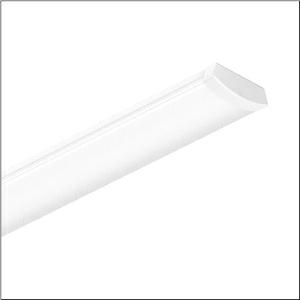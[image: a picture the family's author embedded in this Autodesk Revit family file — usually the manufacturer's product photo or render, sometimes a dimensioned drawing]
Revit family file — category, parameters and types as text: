
# Revit family: siluette_21_51ln12mdm20a
name_source: partatom
category: Lighting Fixtures
units: mm (PartAtom-declared; Revit-internal decimal feet)

## family parameters
Cut with Voids When Loaded = No
Host = Face
Light Source = No
Part Type = Normal
Room Calculation Point = No
Round Connector Dimension = Use Diameter
Shared = No

## types (1)
- --- (1 x LED, 1510 lm, 12.2 W, 5000K)
    Apparent Load = 12 VA
    CIE Flux Codes = 43 73 92 94 100
    Color Rendering = 80
    Color Temperature = 5000K
    Default Elevation = 1800 mm
    Description = Siluette 21, office luminaire, primary optical cover: enclosure, of PC, frosted, light emission: direct distribution, primary light characteristic: symmetric, installation type: suspended mounting, surface-mounted, LED, rated luminous flux: 2.630lm, luminous efficacy: 135lm/W, light colour: 830/840/850, colour temperature: 3000/4000/5000K, control gear: ON/OFF Multilumen, with terminal, 3-pole, mains connection: 220..240V, AC, 50/60Hz, rated input power: 20W, housing, of sheet steel, white, length: 600mm, width: 152mm, height: 53mm, end cap, of PMMA, white, protection rating (complete): IP44, insulation class (complete): insulation class I (protective earthing), certification: CE, UKCA, protection symbol: D, impact resistance: IK04, permissible operating ambient temperature: -20..+40°C, contact your sales advisor before using the luminaires in applications with unclear chemical exposure, large temperature fluctuations or condensation-forming humidity, corresponds to IFS (International Featured Standards) requirements for safety and quality in the food industry, packaging unit: 1 piece
    Height = 52 mm  [stored 0.170604 ft]
    Lamp = 1 x LED
    Lamp Light Flux = 1510 lm
    Lamp Power = 12.2 W
    Lamp count = 1
    Length = 645 mm
    Luminous efficacy = 124 lm/W
    Manufacturer = Siteco
    ModVariant = No
    Model = 51LN12MDM20A
    Mounting Place = Ceiling
    Mounting Type = Pendant
    Number of Poles = 1
    OnlyDefault = Yes
    Power Factor = 1
    Product Name = Siluette 21
    Product group = office luminaire | ceiling pendant
    ProductGroupID = 903
    Protection Class = Protection class I
    Protection Degree = IP 44
    RLX_Detail_Level = 1
    RLX_Emergency_Light_Flux = 0 lm
    RLX_Emergency_Type = 0
    RLX_Emergency_Type_DB = No
    RlxData = <blob elided: 19165 chars, md5=18696f39>
    Socket = socket
    Standby Power = 0 W
    System Light Flux = 1510 lm
    System Power = 12 W
    Type Comments = individual setting: colour temperature 5000K, luminous flux: 58 % | (OFF | OFF | ON) | 200 mA
    Type Image = l_1296910.jpg
    URL = http://relux.com
    VarID = @adj_067433
    Voltage = 0 V
    Weight = 0.00 kg
    Width = 152 mm

note: [stored X ft] marks values corroborated as IEEE doubles in the binary element streams (Revit-internal decimal feet)

## geometry (parser evidence)
native form markers: Blend x4, Sweep x12
no freeform markers — native parametric forms only
